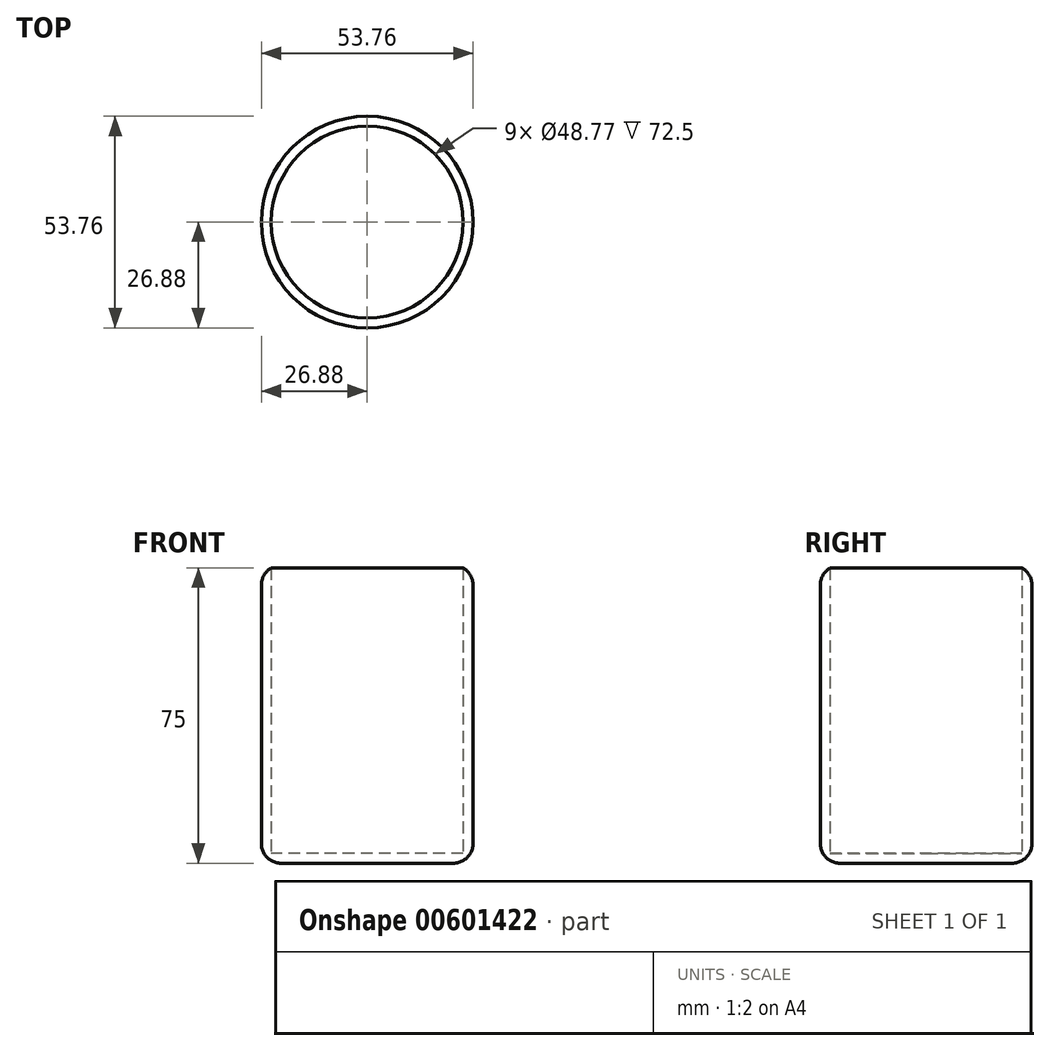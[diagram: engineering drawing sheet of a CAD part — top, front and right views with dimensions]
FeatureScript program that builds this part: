
annotation { "Feature Type Name" : "Feature", "Feature Type Description" : "" }
export const myFeature = defineFeature(function(context is Context, id is Id, definition is map)
    precondition{}
    {
        {
            var Q0;
            Q0=qCreatedBy(makeId("Top.planeOp"),FACE);
            var sketch = newSketch(context, id + "F0", { "sketchPlane" : qUnion([Q0])});
            skCircle(sketch, "E0", {"center": v(0, 0) * mm, "radius": 26.88 * mm});
            skLineSegment(sketch, "E1", {"start": v(0, 0) * mm, "end": v(0, 0) * mm});
            skSolve(sketch);
        }
        {
            var Q0;
            Q0 = qSketchRegion(id + "F0", true);
            extrude(context, id + "F1", {"entities" : qUnion([Q0]), "depth" : 75 * mm, "offsetDistance" : 25 * mm});
        }
        {
            var Q0;
            Q0=makeQuery(id+"F1.opExtrude","CAP_FACE",FACE,{"disambiguationData":[OSD([sQuery(id+"F0.wireOp",EDGE,"E0")])],"isStart":false});
            shell(context, id + "F2", {"entities" : qUnion([Q0]), "thickness" : 2.5 * mm});
        }
        {
            var Q0;
            Q0=makeQuery(id+"F1.opExtrude","CAP_EDGE",EDGE,{"disambiguationData":[OSD([sQuery(id+"F0.wireOp",EDGE,"E0")])],"isStart":false});
            fillet(context, id + "F3", {"entities" : qUnion([Q0]), "radius" : 5 * mm, "tangentPropagation" : true, "allowEdgeOverflow" : false});
        }
        {
            var Q0;
            Q0=makeQuery(id+"F1.opExtrude","CAP_EDGE",EDGE,{"disambiguationData":[OSD([sQuery(id+"F0.wireOp",EDGE,"E0")])],"isStart":true});
            fillet(context, id + "F4", {"entities" : qUnion([Q0]), "radius" : 5 * mm, "tangentPropagation" : true, "allowEdgeOverflow" : false});
        }
    });
